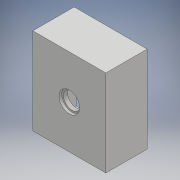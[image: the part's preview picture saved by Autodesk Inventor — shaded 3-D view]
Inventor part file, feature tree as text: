
AUTODESK INVENTOR PART (.ipt)
format: ipt  version: 2018 (Build 220112000, 112)  size: 116,224 bytes
history: native  units: mm
features: extrude x4, sketch x4
ambient origin geometry x8: Origin, YZ Plane, XZ Plane, XY Plane, X Axis, Y Axis, Z Axis, Center Point
bodies: Solid1 (feature_tree)
feature tree (8):
  extrude  "Extrusion1"  Depth=63.0mm
  extrude  "Extrusion2"  Depth=50.0mm
  extrude  "Extrusion3"  Depth=25.0mm TaperAngle=0.0deg
  extrude  "Extrusion4"  Depth=2.0mm TaperAngle=0.0deg
  sketch  "Sketch1"  dims[d0=53.0mm d1=63.0mm]
  sketch  "Sketch2"  dims[d2=30.0mm d3=0.0mm d4=50.0mm]
  sketch  "Sketch3"  dims[d5=60.0mm d6=25.0mm d7=0.0mm]
  sketch  "Sketch4"  dims[d10=15.0mm d11=2.0mm d12=0.0mm d13=12.5mm d14=2.0mm d15=0.0mm]
